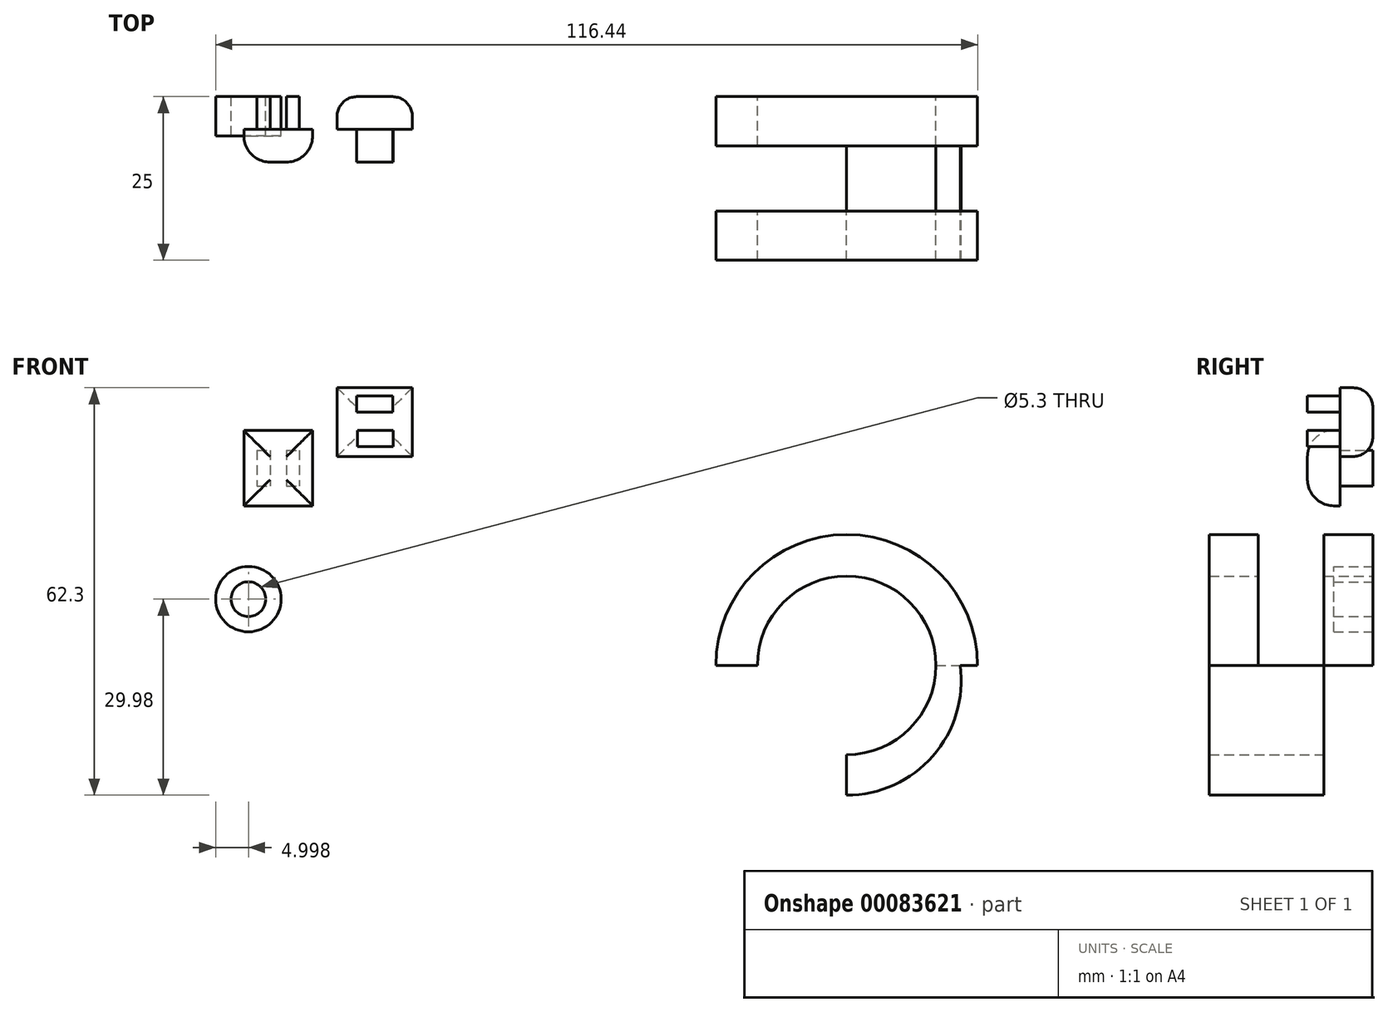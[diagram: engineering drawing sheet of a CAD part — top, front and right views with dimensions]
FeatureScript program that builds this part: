
annotation { "Feature Type Name" : "Feature", "Feature Type Description" : "" }
export const myFeature = defineFeature(function(context is Context, id is Id, definition is map)
    precondition{}
    {
        {
            var Q0;
            Q0=qCreatedBy(makeId("Front.planeOp"),FACE);
            var sketch = newSketch(context, id + "F0", { "sketchPlane" : qUnion([Q0])});
            skCircle(sketch, "E0", {"center": v(-46.05, 41.4) * mm, "radius": 2.65 * mm});
            skCircle(sketch, "E1", {"center": v(-46.05, 41.4) * mm, "radius": 5 * mm});
            skSolve(sketch);
        }
        {
            var Q0;
            Q0 = qSketchRegion(id + "F0", true);
            extrude(context, id + "F1", {"entities" : qUnion([Q0]), "depth" : 6 * mm});
        }
        {
            var Q0;
            Q0=qCreatedBy(makeId("Front.planeOp"),FACE);
            var sketch = newSketch(context, id + "F2", { "sketchPlane" : qUnion([Q0])});
            skLineSegment(sketch, "E2.bottom", {"start": v(-44.74, 64.17) * mm, "end": v(-38.24, 64.17) * mm});
            skLineSegment(sketch, "E2.top", {"start": v(-44.74, 58.67) * mm, "end": v(-38.24, 58.67) * mm});
            skLineSegment(sketch, "E2.left", {"start": v(-44.74, 64.17) * mm, "end": v(-44.74, 58.67) * mm});
            skLineSegment(sketch, "E2.right", {"start": v(-38.24, 64.17) * mm, "end": v(-38.24, 58.67) * mm});
            skLineSegment(sketch, "E3.bottom", {"start": v(-42.74, 64.17) * mm, "end": v(-40.24, 64.17) * mm});
            skLineSegment(sketch, "E3.top", {"start": v(-42.74, 58.67) * mm, "end": v(-40.24, 58.67) * mm});
            skLineSegment(sketch, "E3.left", {"start": v(-42.74, 64.17) * mm, "end": v(-42.74, 58.67) * mm});
            skLineSegment(sketch, "E3.right", {"start": v(-40.24, 64.17) * mm, "end": v(-40.24, 58.67) * mm});
            skSolve(sketch);
        }
        {
            var Q0;
            {var subQ0=sQuery(id+"F2.wireOp",EDGE,"E2.right");Q0=makeQuery(id+"F2.imprint","IMPRINT",FACE,{"disambiguationData":[TD([[makeQuery(id+"F2.imprint","IMPRINT",EDGE,{"derivedFrom":subQ0}),-1.0]])]});}
            var Q1;
            {var subQ0=sQuery(id+"F2.wireOp",EDGE,"E2.left");Q1=makeQuery(id+"F2.imprint","IMPRINT",FACE,{"disambiguationData":[TD([[makeQuery(id+"F2.imprint","IMPRINT",EDGE,{"derivedFrom":subQ0}),1.0]])]});}
            extrude(context, id + "F3", {"entities" : qUnion([Q0, Q1]), "depth" : 5 * mm});
        }
        {
            var Q0;
            Q0=makeQuery(id+"F3.opExtrude","CAP_FACE",FACE,{"disambiguationData":[OSD([sQuery(id+"F2.wireOp",EDGE,"E2.bottom"),sQuery(id+"F2.wireOp",EDGE,"E2.top"),sQuery(id+"F2.wireOp",EDGE,"E2.left"),sQuery(id+"F2.wireOp",EDGE,"E3.left")])],"isStart":false});
            var sketch = newSketch(context, id + "F4", { "sketchPlane" : qUnion([Q0])});
            skLineSegment(sketch, "E4.bottom", {"start": v(-46.74, 67.17) * mm, "end": v(-36.24, 67.17) * mm});
            skLineSegment(sketch, "E4.top", {"start": v(-46.74, 55.67) * mm, "end": v(-36.24, 55.67) * mm});
            skLineSegment(sketch, "E4.left", {"start": v(-46.74, 67.17) * mm, "end": v(-46.74, 55.67) * mm});
            skLineSegment(sketch, "E4.right", {"start": v(-36.24, 67.17) * mm, "end": v(-36.24, 55.67) * mm});
            skSolve(sketch);
        }
        {
            var Q0;
            Q0 = qSketchRegion(id + "F4", true);
            extrude(context, id + "F5", {"entities" : qUnion([Q0]), "depth" : 5 * mm});
        }
        {
            var Q0;
            Q0=makeQuery(id+"F5.opExtrude","CAP_FACE",FACE,{"disambiguationData":[OSD([sQuery(id+"F4.wireOp",EDGE,"E4.bottom"),sQuery(id+"F4.wireOp",EDGE,"E4.top"),sQuery(id+"F4.wireOp",EDGE,"E4.left"),sQuery(id+"F4.wireOp",EDGE,"E4.right")])],"isStart":false});
            fillet(context, id + "F6", {"entities" : qUnion([Q0]), "radius" : 4 * mm, "tangentPropagation" : true, "allowEdgeOverflow" : false});
        }
        {
            var Q0;
            Q0=qCreatedBy(makeId("Front.planeOp"),FACE);
            var sketch = newSketch(context, id + "F7", { "sketchPlane" : qUnion([Q0])});
            skLineSegment(sketch, "E5.bottom", {"start": v(-32.5, 73.72) * mm, "end": v(-21, 73.72) * mm});
            skLineSegment(sketch, "E5.top", {"start": v(-32.5, 63.22) * mm, "end": v(-21, 63.22) * mm});
            skLineSegment(sketch, "E5.left", {"start": v(-32.5, 73.72) * mm, "end": v(-32.5, 63.22) * mm});
            skLineSegment(sketch, "E5.right", {"start": v(-21, 73.72) * mm, "end": v(-21, 63.22) * mm});
            skSolve(sketch);
        }
        {
            var Q0;
            Q0 = qSketchRegion(id + "F7", true);
            extrude(context, id + "F8", {"entities" : qUnion([Q0]), "depth" : 5 * mm});
        }
        {
            var Q0;
            Q0=makeQuery(id+"F8.opExtrude","CAP_FACE",FACE,{"disambiguationData":[OSD([sQuery(id+"F7.wireOp",EDGE,"E5.bottom"),sQuery(id+"F7.wireOp",EDGE,"E5.top"),sQuery(id+"F7.wireOp",EDGE,"E5.left"),sQuery(id+"F7.wireOp",EDGE,"E5.right")])],"isStart":false});
            var sketch = newSketch(context, id + "F9", { "sketchPlane" : qUnion([Q0])});
            skLineSegment(sketch, "E6.bottom", {"start": v(-29.5, 72.47) * mm, "end": v(-24, 72.47) * mm});
            skLineSegment(sketch, "E6.top", {"start": v(-29.5, 69.97) * mm, "end": v(-24, 69.97) * mm});
            skLineSegment(sketch, "E6.left", {"start": v(-29.5, 72.47) * mm, "end": v(-29.5, 69.97) * mm});
            skLineSegment(sketch, "E6.right", {"start": v(-24, 72.47) * mm, "end": v(-24, 69.97) * mm});
            skLineSegment(sketch, "E7.bottom", {"start": v(-29.4, 67.22) * mm, "end": v(-23.9, 67.22) * mm});
            skLineSegment(sketch, "E7.top", {"start": v(-29.4, 64.72) * mm, "end": v(-23.9, 64.72) * mm});
            skLineSegment(sketch, "E7.left", {"start": v(-29.4, 67.22) * mm, "end": v(-29.4, 64.72) * mm});
            skLineSegment(sketch, "E7.right", {"start": v(-23.9, 67.22) * mm, "end": v(-23.9, 64.72) * mm});
            skSolve(sketch);
        }
        {
            var Q0;
            Q0 = qSketchRegion(id + "F9", true);
            extrude(context, id + "F10", {"entities" : qUnion([Q0]), "operationType" : NewBodyOperationType.ADD, "depth" : 5 * mm});
        }
        {
            var Q0;
            Q0=makeQuery(id+"F8.opExtrude","CAP_FACE",FACE,{"disambiguationData":[OSD([sQuery(id+"F7.wireOp",EDGE,"E5.bottom"),sQuery(id+"F7.wireOp",EDGE,"E5.top"),sQuery(id+"F7.wireOp",EDGE,"E5.left"),sQuery(id+"F7.wireOp",EDGE,"E5.right")])],"isStart":true});
            fillet(context, id + "F11", {"entities" : qUnion([Q0]), "radius" : 3 * mm, "tangentPropagation" : true, "allowEdgeOverflow" : false});
        }
        {
            var Q0;
            Q0=qCreatedBy(makeId("Front.planeOp"),FACE);
            var sketch = newSketch(context, id + "F12", { "sketchPlane" : qUnion([Q0])});
            skCircle(sketch, "E8", {"center": v(45.39, 31.27) * mm, "radius": 13.65 * mm});
            skCircle(sketch, "E9", {"center": v(45.39, 31.27) * mm, "radius": 20 * mm});
            skLineSegment(sketch, "E10.bottom", {"start": v(45.39, 31.27) * mm, "end": v(65.39, 31.27) * mm});
            skLineSegment(sketch, "E10.top", {"start": v(45.39, 51.27) * mm, "end": v(65.39, 51.27) * mm});
            skLineSegment(sketch, "E10.left", {"start": v(45.39, 31.27) * mm, "end": v(45.39, 51.27) * mm});
            skLineSegment(sketch, "E10.right", {"start": v(65.39, 31.27) * mm, "end": v(65.39, 51.27) * mm});
            skPoint(sketch, "E11.oppositeSnap0", {"position": v(55.39, 51.27) * mm});
            skLineSegment(sketch, "E11.bottom", {"start": v(45.39, 31.27) * mm, "end": v(25.39, 31.27) * mm});
            skLineSegment(sketch, "E11.top", {"start": v(45.39, 51.27) * mm, "end": v(25.39, 51.27) * mm});
            skLineSegment(sketch, "E11.right", {"start": v(25.39, 31.27) * mm, "end": v(25.39, 51.27) * mm});
            skSolve(sketch);
        }
        {
            var Q0;
            {var subQ2=sQuery(id+"F12.wireOp",EDGE,"E10.top");Q0=makeQuery(id+"F12.imprint","IMPRINT",FACE,{"disambiguationData":[TD([[makeQuery(id+"F12.imprint","IMPRINT",EDGE,{"derivedFrom":subQ2}),-1.0]])]});}
            var Q1;
            {var subQ0=sQuery(id+"F12.wireOp",EDGE,"E11.top");Q1=makeQuery(id+"F12.imprint","IMPRINT",FACE,{"disambiguationData":[TD([[makeQuery(id+"F12.imprint","IMPRINT",EDGE,{"derivedFrom":subQ0}),1.0]])]});}
            var Q2;
            {var subQ0=sQuery(id+"F12.wireOp",EDGE,"E10.left");var subQ1=sQuery(id+"F12.wireOp",EDGE,"E8");var subQ2=makeQuery(id+"F12.imprint","INTERSECT",VERTEX,{"derivedFrom":[subQ1,subQ0]});Q2=makeQuery(id+"F12.imprint","IMPRINT",FACE,{"disambiguationData":[TD([[makeQuery(id+"F12.imprint","IMPRINT",EDGE,{"disambiguationData":[TD([[subQ2,1.0]])],"derivedFrom":subQ1}),-1.0]])]});}
            var Q3;
            {var subQ0=sQuery(id+"F12.wireOp",EDGE,"E10.left");var subQ1=sQuery(id+"F12.wireOp",EDGE,"E8");var subQ2=makeQuery(id+"F12.imprint","INTERSECT",VERTEX,{"derivedFrom":[subQ1,subQ0]});Q3=makeQuery(id+"F12.imprint","IMPRINT",FACE,{"disambiguationData":[TD([[makeQuery(id+"F12.imprint","IMPRINT",EDGE,{"disambiguationData":[TD([[subQ2,-1.0]])],"derivedFrom":subQ1}),-1.0]])]});}
            extrude(context, id + "F13", {"entities" : qUnion([Q0, Q1, Q2, Q3]), "depth" : 7.5 * mm});
        }
        {
            var Q0;
            Q0=makeQuery(id+"F13.opExtrude","CAP_FACE",FACE,{"disambiguationData":[OSD([sQuery(id+"F12.wireOp",EDGE,"E8"),sQuery(id+"F12.wireOp",EDGE,"E10.bottom"),sQuery(id+"F12.wireOp",EDGE,"E10.top"),sQuery(id+"F12.wireOp",EDGE,"E10.right"),sQuery(id+"F12.wireOp",EDGE,"E11.bottom"),sQuery(id+"F12.wireOp",EDGE,"E11.top"),sQuery(id+"F12.wireOp",EDGE,"E11.right")])],"isStart":false});
            var sketch = newSketch(context, id + "F14", { "sketchPlane" : qUnion([Q0])});
            skLineSegment(sketch, "E12", {"start": v(45.39, 44.92) * mm, "end": v(45.39, 0) * mm});
            skCircle(sketch, "E13", {"center": v(45.39, 28.92) * mm, "radius": 17.5 * mm});
            skCircle(sketch, "E14", {"center": v(45.39, 31.27) * mm, "radius": 13.65 * mm});
            skLineSegment(sketch, "E15", {"start": v(25.39, 31.27) * mm, "end": v(65.39, 31.27) * mm});
            skSolve(sketch);
        }
        {
            var Q0;
            {var subQ0=sQuery(id+"F14.wireOp",EDGE,"E15");var subQ3=sQuery(id+"F14.wireOp",EDGE,"E13");var subQ7=makeQuery(id+"F14.imprint","INTERSECT",VERTEX,{"disambiguationData":[OD(0.0)],"derivedFrom":[subQ3,subQ0]});Q0=makeQuery(id+"F14.imprint","IMPRINT",FACE,{"disambiguationData":[TD([[makeQuery(id+"F14.imprint","IMPRINT",EDGE,{"disambiguationData":[TD([[subQ7,1.0]])],"derivedFrom":subQ3}),1.0]])]});}
            extrude(context, id + "F15", {"entities" : qUnion([Q0]), "operationType" : NewBodyOperationType.ADD, "depth" : 10 * mm});
        }
        {
            var Q0;
            Q0=makeQuery(id+"F15.opExtrude","CAP_FACE",FACE,{"disambiguationData":[OSD([sQuery(id+"F14.wireOp",EDGE,"E13"),sQuery(id+"F14.wireOp",EDGE,"E14"),sQuery(id+"F14.wireOp",EDGE,"E15")])],"isStart":false});
            var sketch = newSketch(context, id + "F16", { "sketchPlane" : qUnion([Q0])});
            skLineSegment(sketch, "E16.bottom", {"start": v(25.39, 31.27) * mm, "end": v(65.39, 31.27) * mm});
            skLineSegment(sketch, "E16.top", {"start": v(25.39, 51.28) * mm, "end": v(65.39, 51.28) * mm});
            skLineSegment(sketch, "E16.left", {"start": v(25.39, 31.27) * mm, "end": v(25.39, 51.28) * mm});
            skLineSegment(sketch, "E16.right", {"start": v(65.39, 31.27) * mm, "end": v(65.39, 51.28) * mm});
            skCircle(sketch, "E17", {"center": v(45.39, 31.27) * mm, "radius": 13.65 * mm});
            skSolve(sketch);
        }
        {
            var Q0;
            Q0=makeQuery(id+"F16.imprint","IMPRINT",FACE,{"disambiguationData":[TD([[makeQuery(id+"F16.imprint","IMPRINT",EDGE,{"derivedFrom":sQuery(id+"F16.wireOp",EDGE,"E16.top")}),-1.0]])]});
            var Q1;
            {var subQ3=makeQuery(id+"F15.opExtrude","CAP_EDGE",EDGE,{"disambiguationData":[OSD([sQuery(id+"F14.wireOp",EDGE,"E13")])],"isStart":false});Q1=makeQuery(id+"F16.imprint","IMPRINT",FACE,{"disambiguationData":[TD([[makeQuery(id+"F16.imprint","IMPRINT",EDGE,{"derivedFrom":subQ3}),1.0]])]});}
            extrude(context, id + "F17", {"entities" : qUnion([Q0, Q1]), "operationType" : NewBodyOperationType.ADD, "depth" : 7.5 * mm});
        }
        {
            var Q0;
            Q0=makeQuery(id+"F17.opExtrude","CAP_FACE",FACE,{"disambiguationData":[OSD([sQuery(id+"F16.wireOp",EDGE,"E16.bottom"),sQuery(id+"F16.wireOp",EDGE,"E16.top"),sQuery(id+"F16.wireOp",EDGE,"E16.left"),sQuery(id+"F16.wireOp",EDGE,"E16.right"),sQuery(id+"F16.wireOp",EDGE,"E17")])],"isStart":false});
            var sketch = newSketch(context, id + "F18", { "sketchPlane" : qUnion([Q0])});
            skCircle(sketch, "E18", {"center": v(45.39, 31.27) * mm, "radius": 20 * mm});
            skLineSegment(sketch, "E19.bottom", {"start": v(25.39, 31.27) * mm, "end": v(65.39, 31.27) * mm});
            skLineSegment(sketch, "E19.top", {"start": v(25.39, 51.28) * mm, "end": v(65.39, 51.28) * mm});
            skLineSegment(sketch, "E19.left", {"start": v(25.39, 31.27) * mm, "end": v(25.39, 51.28) * mm});
            skLineSegment(sketch, "E19.right", {"start": v(65.39, 31.27) * mm, "end": v(65.39, 51.28) * mm});
            skSolve(sketch);
        }
        {
            var Q0;
            Q0=makeQuery(id+"F18.imprint","IMPRINT",FACE,{"disambiguationData":[TD([[makeQuery(id+"F18.imprint","IMPRINT",EDGE,{"derivedFrom":sQuery(id+"F18.wireOp",EDGE,"E19.top")}),-1.0]])]});
            extrude(context, id + "F19", {"entities" : qUnion([Q0]), "operationType" : NewBodyOperationType.REMOVE, "oppositeDirection" : true, "depth" : 25 * mm});
        }
    });
